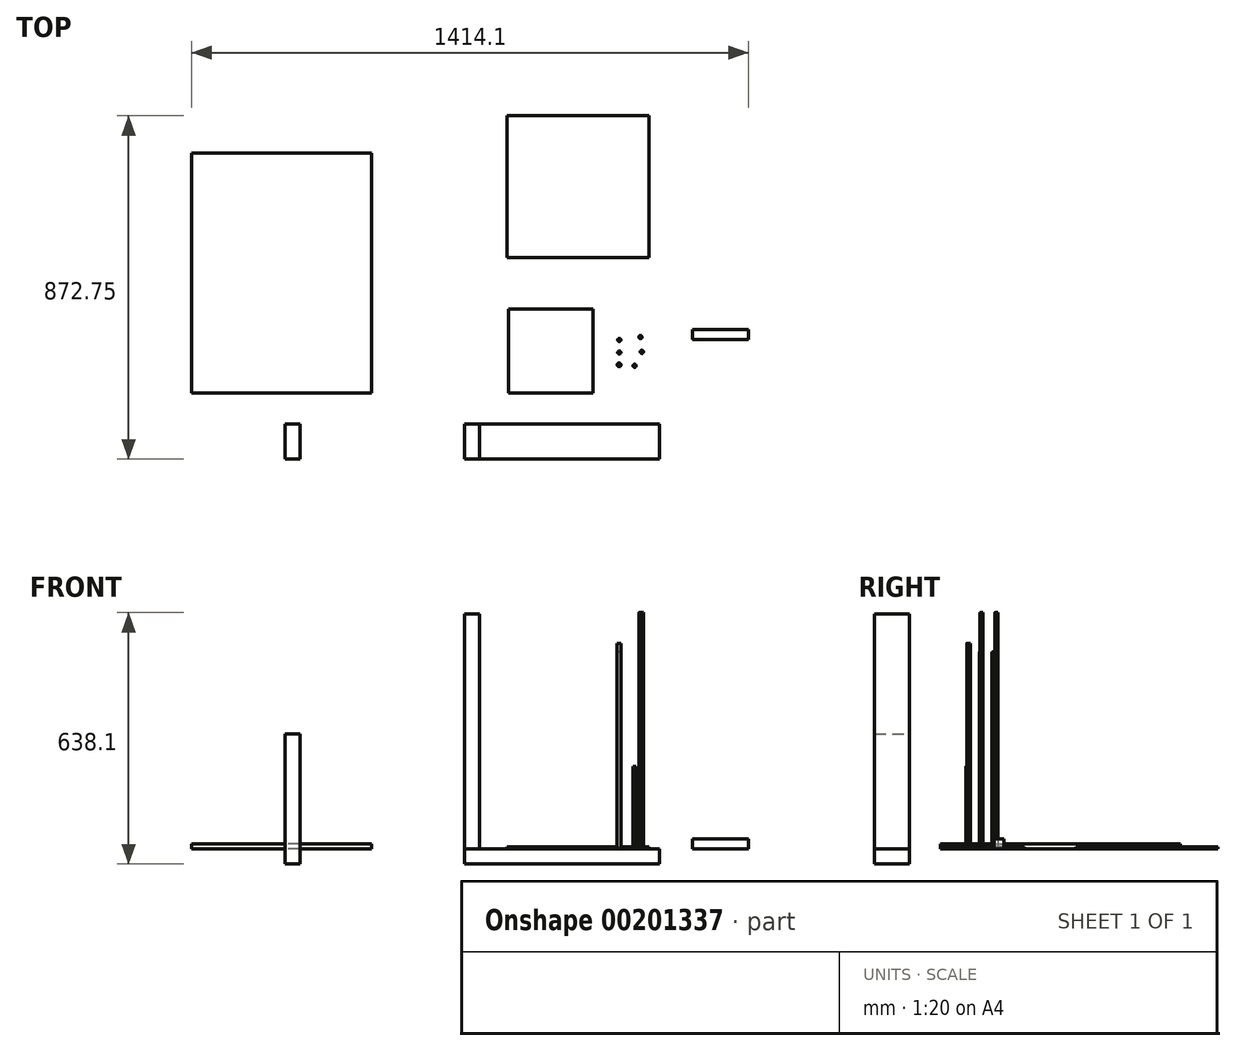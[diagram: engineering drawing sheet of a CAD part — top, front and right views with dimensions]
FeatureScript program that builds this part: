
annotation { "Feature Type Name" : "Feature", "Feature Type Description" : "" }
export const myFeature = defineFeature(function(context is Context, id is Id, definition is map)
    precondition{}
    {
        {
            var Q0;
            Q0=qCreatedBy(makeId("Front.planeOp"),FACE);
            var sketch = newSketch(context, id + "F0", { "sketchPlane" : qUnion([Q0])});
            skLineSegment(sketch, "E0.bottom", {"start": v(0, 596.9) * mm, "end": v(38.1, 596.9) * mm});
            skLineSegment(sketch, "E0.top", {"start": v(0, 0) * mm, "end": v(38.1, 0) * mm});
            skLineSegment(sketch, "E0.left", {"start": v(0, 596.9) * mm, "end": v(0, 0) * mm});
            skLineSegment(sketch, "E0.right", {"start": v(38.1, 596.9) * mm, "end": v(38.1, 0) * mm});
            skLineSegment(sketch, "E1.bottom", {"start": v(0, 0) * mm, "end": v(495.3, 0) * mm});
            skLineSegment(sketch, "E1.top", {"start": v(0, -38.1) * mm, "end": v(495.3, -38.1) * mm});
            skLineSegment(sketch, "E1.left", {"start": v(0, 0) * mm, "end": v(0, -38.1) * mm});
            skLineSegment(sketch, "E1.right", {"start": v(495.3, 0) * mm, "end": v(495.3, -38.1) * mm});
            skLineSegment(sketch, "E2.bottom", {"start": v(-417.94, -38.1) * mm, "end": v(-456.04, -38.1) * mm});
            skLineSegment(sketch, "E2.top", {"start": v(-417.94, 292.1) * mm, "end": v(-456.04, 292.1) * mm});
            skLineSegment(sketch, "E2.left", {"start": v(-417.94, -38.1) * mm, "end": v(-417.94, 292.1) * mm});
            skLineSegment(sketch, "E2.right", {"start": v(-456.04, -38.1) * mm, "end": v(-456.04, 292.1) * mm});
            skSolve(sketch);
        }
        {
            var Q0;
            Q0=makeQuery(id+"F0.imprint","IMPRINT",FACE,{"disambiguationData":[TD([[makeQuery(id+"F0.imprint","IMPRINT",EDGE,{"derivedFrom":sQuery(id+"F0.wireOp",EDGE,"E0.bottom")}),-1.0]])]});
            extrude(context, id + "F1", {"entities" : qUnion([Q0]), "depth" : 88.9 * mm});
        }
        {
            var Q0;
            Q0=makeQuery(id+"F0.imprint","IMPRINT",FACE,{"disambiguationData":[TD([[makeQuery(id+"F0.imprint","IMPRINT",EDGE,{"derivedFrom":sQuery(id+"F0.wireOp",EDGE,"E1.top")}),1.0]])]});
            extrude(context, id + "F2", {"entities" : qUnion([Q0]), "depth" : 88.9 * mm});
        }
        {
            var Q0;
            Q0=qCreatedBy(makeId("Top.planeOp"),FACE);
            var sketch = newSketch(context, id + "F3", { "sketchPlane" : qUnion([Q0])});
            skLineSegment(sketch, "E3.bottom", {"start": v(112.24, 293.13) * mm, "end": v(326.24, 293.13) * mm});
            skLineSegment(sketch, "E3.top", {"start": v(112.24, 79.13) * mm, "end": v(326.24, 79.13) * mm});
            skLineSegment(sketch, "E3.left", {"start": v(112.24, 293.13) * mm, "end": v(112.24, 79.13) * mm});
            skLineSegment(sketch, "E3.right", {"start": v(326.24, 293.13) * mm, "end": v(326.24, 79.13) * mm});
            skCircle(sketch, "E4", {"center": v(393.46, 214.2) * mm, "radius": 4 * mm});
            skCircle(sketch, "E5", {"center": v(393.46, 182.2) * mm, "radius": 4 * mm});
            skLineSegment(sketch, "E6.bottom", {"start": v(108.47, 423.85) * mm, "end": v(468.47, 423.85) * mm});
            skLineSegment(sketch, "E6.top", {"start": v(108.47, 783.85) * mm, "end": v(468.47, 783.85) * mm});
            skLineSegment(sketch, "E6.left", {"start": v(108.47, 423.85) * mm, "end": v(108.47, 783.85) * mm});
            skLineSegment(sketch, "E6.right", {"start": v(468.47, 423.85) * mm, "end": v(468.47, 783.85) * mm});
            skCircle(sketch, "E7", {"center": v(393, 150.76) * mm, "radius": 4.76 * mm});
            skCircle(sketch, "E8", {"center": v(450.7, 183.86) * mm, "radius": 4 * mm});
            skCircle(sketch, "E9", {"center": v(432.52, 148.38) * mm, "radius": 3.97 * mm});
            skCircle(sketch, "E10", {"center": v(447.07, 221.3) * mm, "radius": 4 * mm});
            skLineSegment(sketch, "E11.bottom", {"start": v(-235.73, 79.05) * mm, "end": v(-692.93, 79.05) * mm});
            skLineSegment(sketch, "E11.top", {"start": v(-235.73, 688.65) * mm, "end": v(-692.93, 688.65) * mm});
            skLineSegment(sketch, "E11.left", {"start": v(-235.73, 79.05) * mm, "end": v(-235.73, 688.65) * mm});
            skLineSegment(sketch, "E11.right", {"start": v(-692.93, 79.05) * mm, "end": v(-692.93, 688.65) * mm});
            skLineSegment(sketch, "E12.bottom", {"start": v(579.17, 240.6) * mm, "end": v(721.17, 240.6) * mm});
            skLineSegment(sketch, "E12.top", {"start": v(579.17, 215.6) * mm, "end": v(721.17, 215.6) * mm});
            skLineSegment(sketch, "E12.left", {"start": v(579.17, 240.6) * mm, "end": v(579.17, 215.6) * mm});
            skLineSegment(sketch, "E12.right", {"start": v(721.17, 240.6) * mm, "end": v(721.17, 215.6) * mm});
            skSolve(sketch);
        }
        {
            var Q0;
            Q0=makeQuery(id+"F3.imprint","IMPRINT",FACE,{"disambiguationData":[TD([[makeQuery(id+"F3.imprint","IMPRINT",EDGE,{"derivedFrom":sQuery(id+"F3.wireOp",EDGE,"E3.bottom")}),-1.0]])]});
            extrude(context, id + "F4", {"entities" : qUnion([Q0]), "depth" : 5 * mm});
        }
        {
            var Q0;
            Q0=makeQuery(id+"F3.imprint","IMPRINT",FACE,{"disambiguationData":[TD([[makeQuery(id+"F3.imprint","IMPRINT",EDGE,{"derivedFrom":sQuery(id+"F3.wireOp",EDGE,"E4")}),1.0]])]});
            extrude(context, id + "F5", {"entities" : qUnion([Q0]), "depth" : 500 * mm});
        }
        {
            var Q0;
            Q0=makeQuery(id+"F3.imprint","IMPRINT",FACE,{"disambiguationData":[TD([[makeQuery(id+"F3.imprint","IMPRINT",EDGE,{"derivedFrom":sQuery(id+"F3.wireOp",EDGE,"E5")}),1.0]])]});
            extrude(context, id + "F6", {"entities" : qUnion([Q0]), "depth" : 500 * mm});
        }
        {
            var Q0;
            Q0=makeQuery(id+"F3.imprint","IMPRINT",FACE,{"disambiguationData":[TD([[makeQuery(id+"F3.imprint","IMPRINT",EDGE,{"derivedFrom":sQuery(id+"F3.wireOp",EDGE,"E6.bottom")}),1.0]])]});
            extrude(context, id + "F7", {"entities" : qUnion([Q0]), "depth" : 5 * mm});
        }
        {
            var Q0;
            Q0=makeQuery(id+"F3.imprint","IMPRINT",FACE,{"disambiguationData":[TD([[makeQuery(id+"F3.imprint","IMPRINT",EDGE,{"derivedFrom":sQuery(id+"F3.wireOp",EDGE,"E7")}),1.0]])]});
            extrude(context, id + "F8", {"entities" : qUnion([Q0]), "depth" : 522 * mm});
        }
        {
            var Q0;
            Q0=makeQuery(id+"F3.imprint","IMPRINT",FACE,{"disambiguationData":[TD([[makeQuery(id+"F3.imprint","IMPRINT",EDGE,{"derivedFrom":sQuery(id+"F3.wireOp",EDGE,"E8")}),1.0]])]});
            extrude(context, id + "F9", {"entities" : qUnion([Q0]), "depth" : 600 * mm});
        }
        {
            var Q0;
            Q0=makeQuery(id+"F3.imprint","IMPRINT",FACE,{"disambiguationData":[TD([[makeQuery(id+"F3.imprint","IMPRINT",EDGE,{"derivedFrom":sQuery(id+"F3.wireOp",EDGE,"E9")}),1.0]])]});
            var Q1;
            Q1=sQuery(id+"F3.wireOp",EDGE,"E9");
            extrude(context, id + "F10", {"entities" : qUnion([Q0]), "surfaceEntities" : qUnion([Q1]), "depth" : 210 * mm});
        }
        {
            var Q0;
            Q0=makeQuery(id+"F3.imprint","IMPRINT",FACE,{"disambiguationData":[TD([[makeQuery(id+"F3.imprint","IMPRINT",EDGE,{"derivedFrom":sQuery(id+"F3.wireOp",EDGE,"E10")}),1.0]])]});
            extrude(context, id + "F11", {"entities" : qUnion([Q0]), "depth" : 600 * mm});
        }
        {
            var Q0;
            Q0=makeQuery(id+"F3.imprint","IMPRINT",FACE,{"disambiguationData":[TD([[makeQuery(id+"F3.imprint","IMPRINT",EDGE,{"derivedFrom":sQuery(id+"F3.wireOp",EDGE,"E11.bottom")}),-1.0]])]});
            extrude(context, id + "F12", {"entities" : qUnion([Q0]), "depth" : 12 * mm});
        }
        {
            var Q0;
            Q0=makeQuery(id+"F3.imprint","IMPRINT",FACE,{"disambiguationData":[TD([[makeQuery(id+"F3.imprint","IMPRINT",EDGE,{"derivedFrom":sQuery(id+"F3.wireOp",EDGE,"E12.bottom")}),-1.0]])]});
            extrude(context, id + "F13", {"entities" : qUnion([Q0]), "depth" : 25 * mm});
        }
        {
            var Q0;
            Q0=makeQuery(id+"F0.imprint","IMPRINT",FACE,{"disambiguationData":[TD([[makeQuery(id+"F0.imprint","IMPRINT",EDGE,{"derivedFrom":sQuery(id+"F0.wireOp",EDGE,"E2.bottom")}),-1.0]])]});
            extrude(context, id + "F14", {"entities" : qUnion([Q0]), "depth" : 88.9 * mm});
        }
    });
